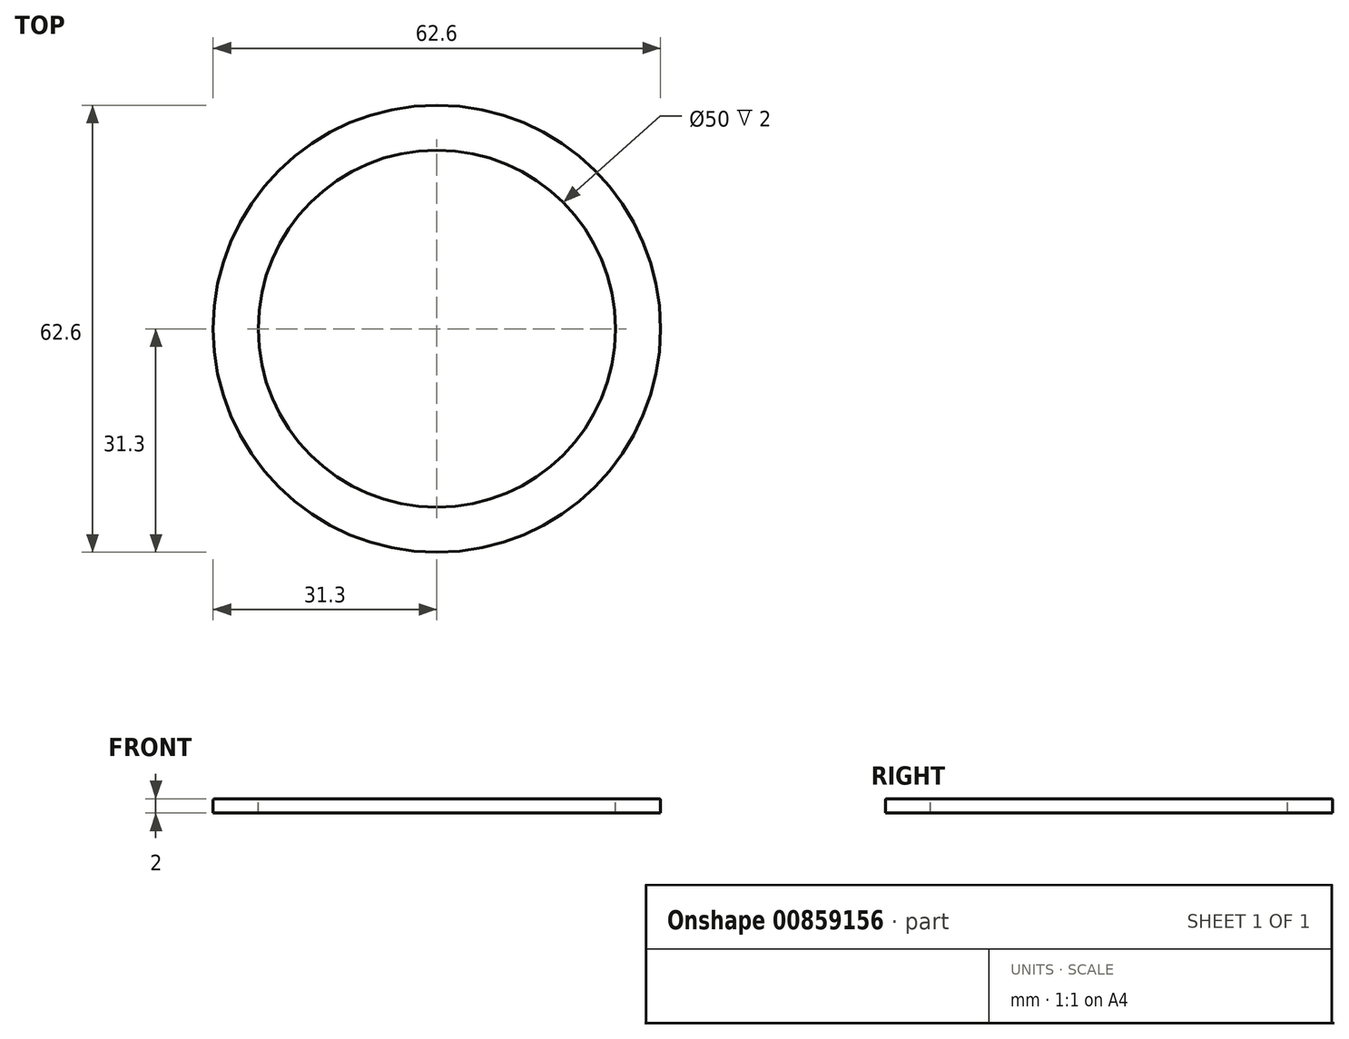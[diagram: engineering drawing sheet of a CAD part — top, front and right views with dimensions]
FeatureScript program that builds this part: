
annotation { "Feature Type Name" : "Feature", "Feature Type Description" : "" }
export const myFeature = defineFeature(function(context is Context, id is Id, definition is map)
    precondition{}
    {
        {
            var Q0;
            Q0=qCreatedBy(makeId("Top.planeOp"),FACE);
            var sketch = newSketch(context, id + "F0", { "sketchPlane" : qUnion([Q0])});
            skCircle(sketch, "E0", {"center": v(0, 0) * mm, "radius": 31.3 * mm});
            skSolve(sketch);
        }
        {
            var Q0;
            Q0 = qSketchRegion(id + "F0", true);
            extrude(context, id + "F1", {"entities" : qUnion([Q0]), "depth" : 2 * mm, "offsetDistance" : 25.4 * mm});
        }
        {
            var Q0;
            Q0=makeQuery(id+"F1.opExtrude","CAP_FACE",FACE,{"disambiguationData":[OSD([sQuery(id+"F0.wireOp",EDGE,"E0")])],"isStart":false});
            var sketch = newSketch(context, id + "F2", { "sketchPlane" : qUnion([Q0])});
            skCircle(sketch, "E1", {"center": v(0, 0) * mm, "radius": 25 * mm});
            skSolve(sketch);
        }
        {
            var Q0;
            Q0 = qSketchRegion(id + "F2", true);
            extrude(context, id + "F3", {"entities" : qUnion([Q0]), "operationType" : NewBodyOperationType.REMOVE, "oppositeDirection" : true, "depth" : 2 * mm, "offsetDistance" : 25.4 * mm});
        }
        {
            var Q0;
            Q0=makeQuery(id+"F1.opExtrude","CAP_EDGE",EDGE,{"disambiguationData":[OSD([sQuery(id+"F0.wireOp",EDGE,"E0")])],"isStart":false});
            var Q1;
            Q1=makeQuery(id+"F3.boolean.opBoolean","COPY",EDGE,{"derivedFrom":makeQuery(id+"F3.opExtrude","CAP_EDGE",EDGE,{"disambiguationData":[OSD([sQuery(id+"F2.wireOp",EDGE,"E1")])],"isStart":true})});
            fillet(context, id + "F4", {"entities" : qUnion([Q0, Q1]), "radius" : 0.2 * mm, "tangentPropagation" : true, "allowEdgeOverflow" : false});
        }
    });
